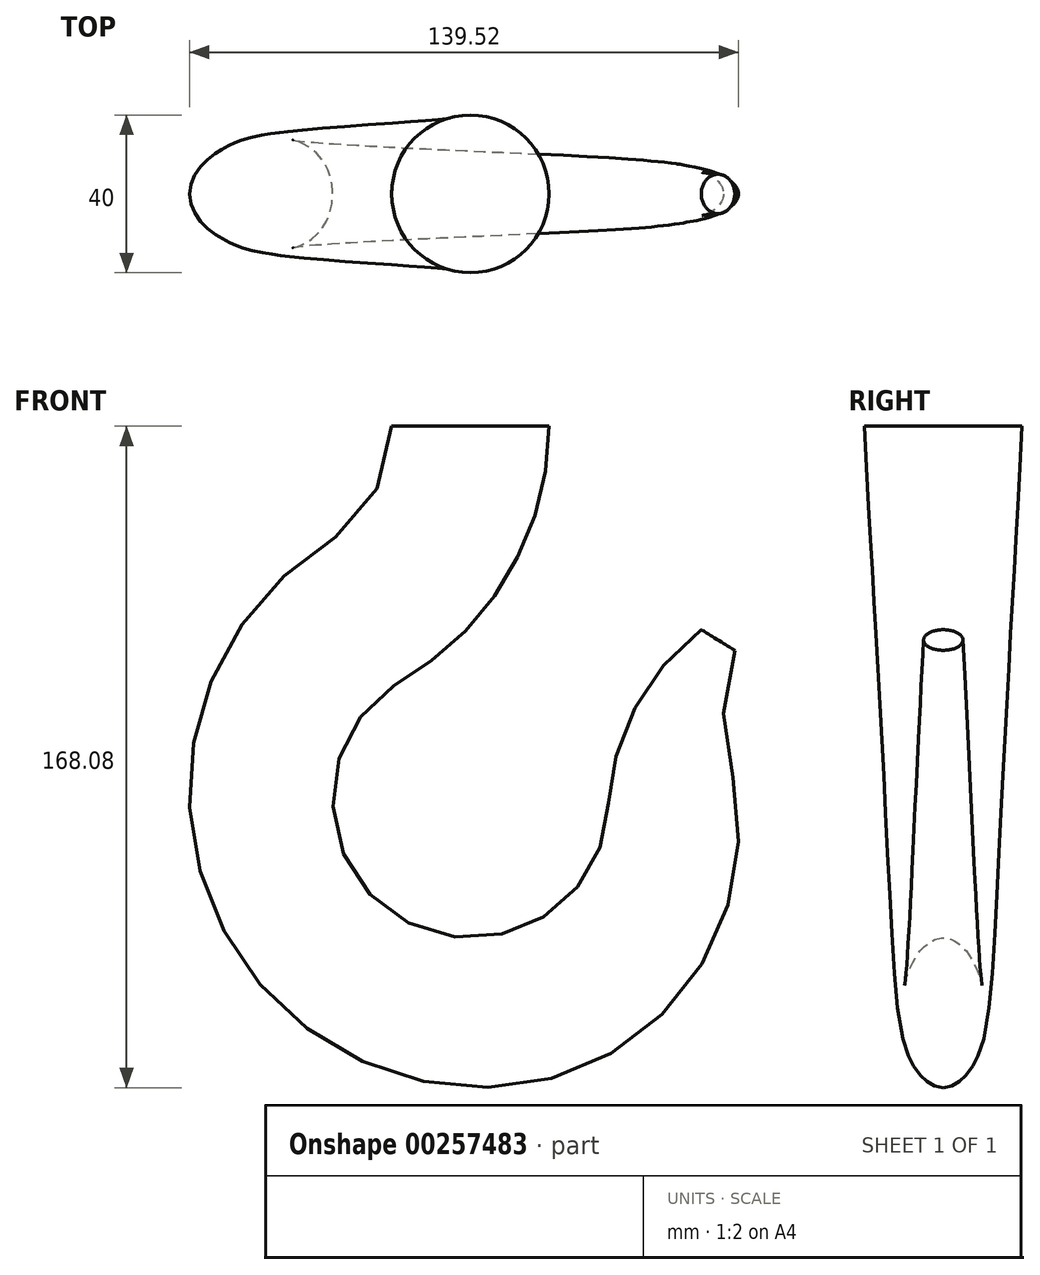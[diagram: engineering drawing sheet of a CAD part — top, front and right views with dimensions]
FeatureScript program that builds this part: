
annotation { "Feature Type Name" : "Feature", "Feature Type Description" : "" }
export const myFeature = defineFeature(function(context is Context, id is Id, definition is map)
    precondition{}
    {
        {
            var Q0;
            Q0=qCreatedBy(makeId("Front.planeOp"),FACE);
            var sketch = newSketch(context, id + "F0", { "sketchPlane" : qUnion([Q0])});
            skLineSegment(sketch, "E0", {"start": v(0, 0) * mm, "end": v(-40, 0) * mm});
            skLineSegment(sketch, "E1", {"start": v(-20, 0) * mm, "end": v(-20, -168) * mm, "construction": true});
            skArc(sketch, "E2", {"start": v(-56.35, -29.62) * mm, "mid": v(-44.36, -16.92) * mm, "end": v(-40, 0) * mm});
            skArc(sketch, "E3", {"start": v(-36.36, -63.93) * mm, "mid": v(-9.8, -36.72) * mm, "end": v(0, 0) * mm});
            skLineSegment(sketch, "E4", {"start": v(-20, 0) * mm, "end": v(-20, -95) * mm, "construction": true});
            skArc(sketch, "E5", {"start": v(-20, -130) * mm, "mid": v(-53.43, -105.37) * mm, "end": v(-39.82, -66.15) * mm});
            skArc(sketch, "E6", {"start": v(-56.35, -29.62) * mm, "mid": v(-88.93, -112.14) * mm, "end": v(-20, -168) * mm});
            skArc(sketch, "E7", {"start": v(-39.82, -66.15) * mm, "mid": v(-38.1, -65.01) * mm, "end": v(-36.36, -63.93) * mm});
            skArc(sketch, "E8", {"start": v(-20, -168) * mm, "mid": v(33.67, -143.95) * mm, "end": v(45.96, -86.43) * mm});
            skArc(sketch, "E9", {"start": v(-20, -130) * mm, "mid": v(4.3, -120.2) * mm, "end": v(14.98, -96.28) * mm});
            skLineSegment(sketch, "E10", {"start": v(38.64, -51.72) * mm, "end": v(47.15, -56.96) * mm});
            skArc(sketch, "E11", {"start": v(47.15, -56.96) * mm, "mid": v(44.33, -71.6) * mm, "end": v(45.96, -86.43) * mm});
            skArc(sketch, "E12", {"start": v(14.98, -96.28) * mm, "mid": v(21.9, -71.4) * mm, "end": v(38.64, -51.72) * mm});
            skLineSegment(sketch, "E13", {"start": v(47.15, -65.95) * mm, "end": v(47.15, -22.43) * mm, "construction": true});
            skSolve(sketch);
        }
        {
            var Q0;
            Q0=sQuery(id+"F0.wireOp",EDGE,"E10");
            cPlane(context, id + "F1", {"entities" : qUnion([Q0]), "cplaneType" : CPlaneType.LINE_ANGLE, "offset" : 25 * mm, "angle" : 90 * degree, "width" : 150 * mm, "height" : 150 * mm});
        }
        {
            var Q0;
            Q0=qCreatedBy(id+"F1.planeOp",FACE);
            var sketch = newSketch(context, id + "F2", { "sketchPlane" : qUnion([Q0])});
            skLineSegment(sketch, "E14.0", {"start": v(60.02, 0) * mm, "end": v(70.02, 0) * mm, "construction": true});
            skCircle(sketch, "E15", {"center": v(65.02, 0) * mm, "radius": 5 * mm});
            skSolve(sketch);
        }
        {
            var Q0;
            Q0=sQuery(id+"F0.wireOp",EDGE,"E0");
            cPlane(context, id + "F3", {"entities" : qUnion([Q0]), "cplaneType" : CPlaneType.LINE_ANGLE, "offset" : 25 * mm, "angle" : 90 * degree, "width" : 150 * mm, "height" : 150 * mm});
        }
        {
            var Q0;
            Q0=qCreatedBy(id+"F3.planeOp",FACE);
            var sketch = newSketch(context, id + "F4", { "sketchPlane" : qUnion([Q0])});
            skLineSegment(sketch, "E16.0", {"start": v(0, 0) * mm, "end": v(-40, 0) * mm, "construction": true});
            skCircle(sketch, "E17", {"center": v(-20, 0) * mm, "radius": 20 * mm});
            skSolve(sketch);
        }
        {
            var Q0;
            Q0=qCreatedBy(makeId("Front.planeOp"),FACE);
            var sketch = newSketch(context, id + "F5", { "sketchPlane" : qUnion([Q0])});
            skArc(sketch, "E18.0", {"start": v(-56.35, -29.62) * mm, "mid": v(-44.36, -16.92) * mm, "end": v(-40, 0) * mm});
            skArc(sketch, "E19.0", {"start": v(-56.35, -29.62) * mm, "mid": v(-88.93, -112.14) * mm, "end": v(-20, -168) * mm});
            skArc(sketch, "E20.0", {"start": v(-20, -168) * mm, "mid": v(33.67, -143.95) * mm, "end": v(45.96, -86.43) * mm});
            skArc(sketch, "E21.0", {"start": v(47.15, -56.96) * mm, "mid": v(44.33, -71.6) * mm, "end": v(45.96, -86.43) * mm});
            skSolve(sketch);
        }
        {
            var Q0;
            Q0=qCreatedBy(makeId("Front.planeOp"),FACE);
            var sketch = newSketch(context, id + "F6", { "sketchPlane" : qUnion([Q0])});
            skArc(sketch, "E22.0", {"start": v(-36.36, -63.93) * mm, "mid": v(-9.8, -36.72) * mm, "end": v(0, 0) * mm});
            skArc(sketch, "E23.0", {"start": v(-39.82, -66.15) * mm, "mid": v(-38.1, -65.01) * mm, "end": v(-36.36, -63.93) * mm});
            skArc(sketch, "E24.0", {"start": v(-20, -130) * mm, "mid": v(-53.43, -105.37) * mm, "end": v(-39.82, -66.15) * mm});
            skArc(sketch, "E25.0", {"start": v(-20, -130) * mm, "mid": v(4.3, -120.2) * mm, "end": v(14.98, -96.28) * mm});
            skArc(sketch, "E26.0", {"start": v(14.98, -96.28) * mm, "mid": v(21.9, -71.4) * mm, "end": v(38.64, -51.72) * mm});
            skSolve(sketch);
        }
        {
            var Q0;
            Q0=makeQuery(id+"F2.imprint","IMPRINT",FACE,{"disambiguationData":[TD([[makeQuery(id+"F2.imprint","IMPRINT",EDGE,{"derivedFrom":sQuery(id+"F2.wireOp",EDGE,"E15")}),1.0]])]});
            var Q1;
            Q1=makeQuery(id+"F4.imprint","IMPRINT",FACE,{"disambiguationData":[TD([[makeQuery(id+"F4.imprint","IMPRINT",EDGE,{"derivedFrom":sQuery(id+"F4.wireOp",EDGE,"E17")}),1.0]])]});
            var Q2;
            Q2 = qConstructionFilter(qBodyType(qCreatedBy(id + "F5" ,EDGE), BodyType.WIRE), ConstructionObject.NO);
            var Q3;
            Q3 = qConstructionFilter(qBodyType(qCreatedBy(id + "F6" ,EDGE), BodyType.WIRE), ConstructionObject.NO);
            loft(context, id + "F7", {"addGuides" : true, "sheetProfilesArray" : [{ "sheetProfileEntities" : qUnion([Q0]) }, { "sheetProfileEntities" : qUnion([Q1]) }], "guidesArray" : [{ "guideEntities" : qUnion([Q2]), "guideDerivativeType" : LoftGuideDerivativeType.DEFAULT, "guideDerivativeMagnitude" : 1 }, { "guideEntities" : qUnion([Q3]), "guideDerivativeType" : LoftGuideDerivativeType.DEFAULT, "guideDerivativeMagnitude" : 1 }]});
        }
    });
